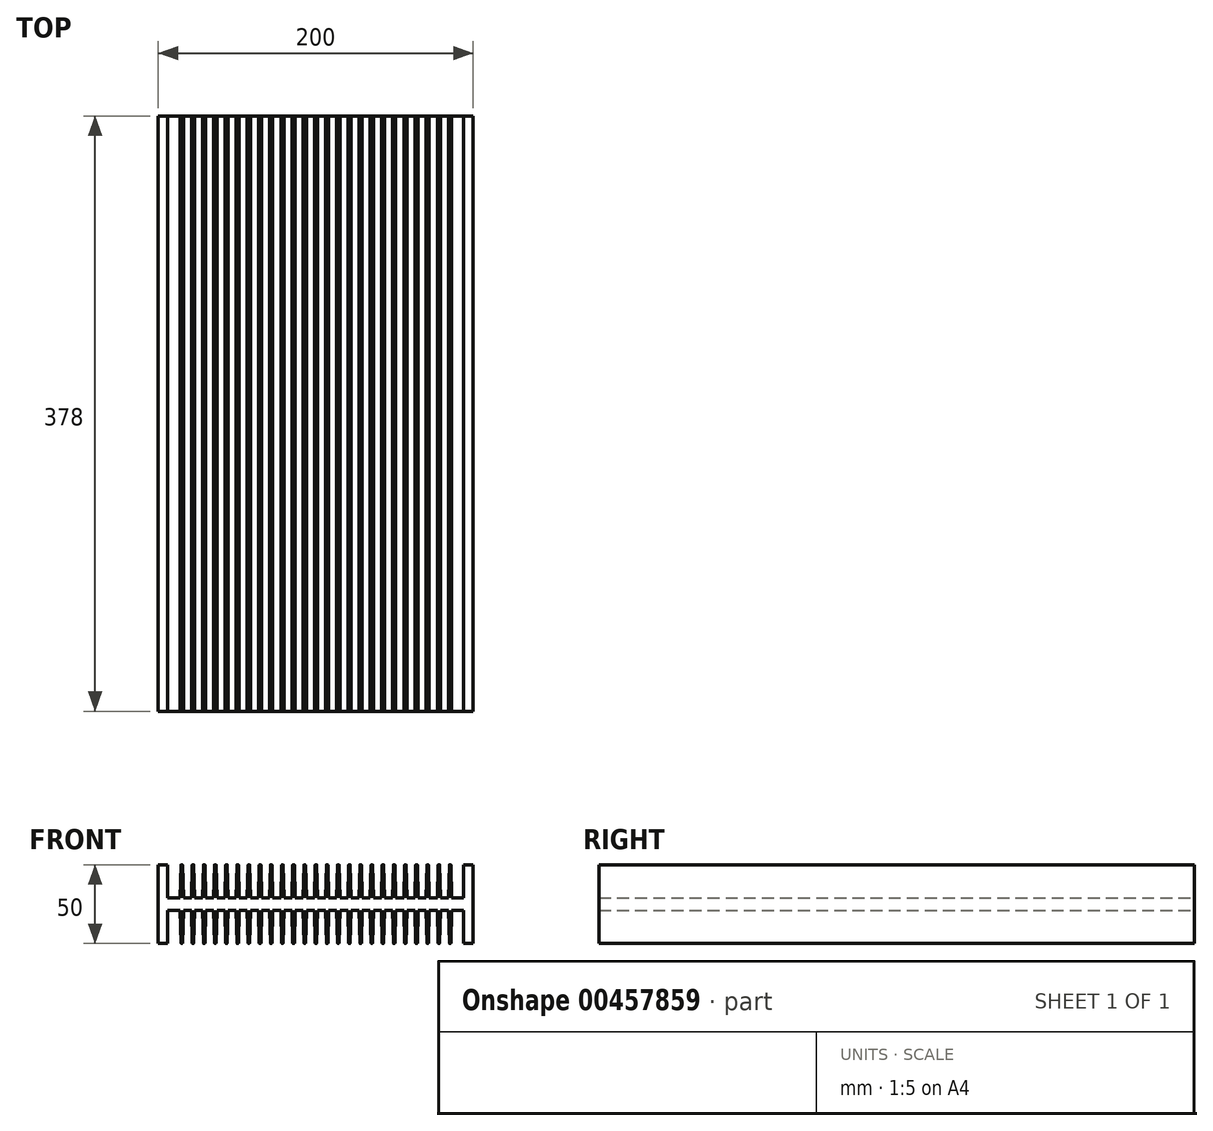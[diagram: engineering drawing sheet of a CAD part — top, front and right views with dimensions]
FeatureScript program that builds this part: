
annotation { "Feature Type Name" : "Feature", "Feature Type Description" : "" }
export const myFeature = defineFeature(function(context is Context, id is Id, definition is map)
    precondition{}
    {
        {
            var Q0;
            Q0=qCreatedBy(makeId("Front.planeOp"),FACE);
            var sketch = newSketch(context, id + "F0", { "sketchPlane" : qUnion([Q0])});
            skLineSegment(sketch, "E0", {"start": v(8, 0) * mm, "end": v(8.5, 20.88) * mm});
            skLineSegment(sketch, "E1", {"start": v(-6, 21) * mm, "end": v(-6, -4) * mm});
            skLineSegment(sketch, "E2", {"start": v(-6, -4) * mm, "end": v(194, -4) * mm});
            skLineSegment(sketch, "E3", {"start": v(194, 21) * mm, "end": v(194, -4) * mm});
            skLineSegment(sketch, "E4", {"start": v(9, 0) * mm, "end": v(9, 21) * mm});
            skLineSegment(sketch, "E5", {"start": v(9, 21) * mm, "end": v(9, 0) * mm, "construction": true});
            skPoint(sketch, "E6.visualSharp", {"position": v(8.5, 21) * mm});
            skArc(sketch, "E6.filletArc", {"start": v(8.62, 21) * mm, "mid": v(8.53, 20.97) * mm, "end": v(8.5, 20.88) * mm});
            skPoint(sketch, "E7.visualSharp", {"position": v(9.5, 21) * mm});
            skLineSegment(sketch, "E8", {"start": v(0, 0) * mm, "end": v(8, 0) * mm});
            skLineSegment(sketch, "E9", {"start": v(10, 0) * mm, "end": v(9.5, 20.88) * mm});
            skLineSegment(sketch, "E10", {"start": v(8.62, 21) * mm, "end": v(9.38, 21) * mm});
            skArc(sketch, "E11.filletArc", {"start": v(9.5, 20.88) * mm, "mid": v(9.47, 20.96) * mm, "end": v(9.38, 21) * mm});
            skLineSegment(sketch, "E12.1.0.1", {"start": v(15.1, 0) * mm, "end": v(15.6, 20.88) * mm});
            skArc(sketch, "E12.1.0.2", {"start": v(15.72, 21) * mm, "mid": v(15.63, 20.97) * mm, "end": v(15.6, 20.88) * mm});
            skLineSegment(sketch, "E12.1.0.3", {"start": v(15.72, 21) * mm, "end": v(16.48, 21) * mm});
            skArc(sketch, "E12.1.0.4", {"start": v(16.6, 20.88) * mm, "mid": v(16.57, 20.96) * mm, "end": v(16.48, 21) * mm});
            skLineSegment(sketch, "E12.1.0.5", {"start": v(17.1, 0) * mm, "end": v(16.6, 20.88) * mm});
            skLineSegment(sketch, "E12.2.0.1", {"start": v(22.2, 0) * mm, "end": v(22.7, 20.88) * mm});
            skArc(sketch, "E12.2.0.2", {"start": v(22.82, 21) * mm, "mid": v(22.73, 20.97) * mm, "end": v(22.7, 20.88) * mm});
            skLineSegment(sketch, "E12.2.0.3", {"start": v(22.82, 21) * mm, "end": v(23.58, 21) * mm});
            skArc(sketch, "E12.2.0.4", {"start": v(23.7, 20.88) * mm, "mid": v(23.67, 20.96) * mm, "end": v(23.58, 21) * mm});
            skLineSegment(sketch, "E12.2.0.5", {"start": v(24.2, 0) * mm, "end": v(23.7, 20.88) * mm});
            skLineSegment(sketch, "E12.3.0.1", {"start": v(29.3, 0) * mm, "end": v(29.8, 20.88) * mm});
            skArc(sketch, "E12.3.0.2", {"start": v(29.92, 21) * mm, "mid": v(29.83, 20.97) * mm, "end": v(29.8, 20.88) * mm});
            skLineSegment(sketch, "E12.3.0.3", {"start": v(29.92, 21) * mm, "end": v(30.68, 21) * mm});
            skArc(sketch, "E12.3.0.4", {"start": v(30.8, 20.88) * mm, "mid": v(30.77, 20.96) * mm, "end": v(30.68, 21) * mm});
            skLineSegment(sketch, "E12.3.0.5", {"start": v(31.3, 0) * mm, "end": v(30.8, 20.88) * mm});
            skLineSegment(sketch, "E12.4.0.1", {"start": v(36.4, 0) * mm, "end": v(36.9, 20.88) * mm});
            skArc(sketch, "E12.4.0.2", {"start": v(37.02, 21) * mm, "mid": v(36.93, 20.97) * mm, "end": v(36.9, 20.88) * mm});
            skLineSegment(sketch, "E12.4.0.3", {"start": v(37.02, 21) * mm, "end": v(37.78, 21) * mm});
            skArc(sketch, "E12.4.0.4", {"start": v(37.9, 20.88) * mm, "mid": v(37.87, 20.96) * mm, "end": v(37.78, 21) * mm});
            skLineSegment(sketch, "E12.4.0.5", {"start": v(38.4, 0) * mm, "end": v(37.9, 20.88) * mm});
            skLineSegment(sketch, "E12.5.0.1", {"start": v(43.5, 0) * mm, "end": v(44, 20.88) * mm});
            skArc(sketch, "E12.5.0.2", {"start": v(44.12, 21) * mm, "mid": v(44.03, 20.97) * mm, "end": v(44, 20.88) * mm});
            skLineSegment(sketch, "E12.5.0.3", {"start": v(44.12, 21) * mm, "end": v(44.88, 21) * mm});
            skArc(sketch, "E12.5.0.4", {"start": v(45, 20.88) * mm, "mid": v(44.97, 20.96) * mm, "end": v(44.88, 21) * mm});
            skLineSegment(sketch, "E12.5.0.5", {"start": v(45.5, 0) * mm, "end": v(45, 20.88) * mm});
            skLineSegment(sketch, "E12.6.0.1", {"start": v(50.6, 0) * mm, "end": v(51.1, 20.88) * mm});
            skArc(sketch, "E12.6.0.2", {"start": v(51.22, 21) * mm, "mid": v(51.13, 20.97) * mm, "end": v(51.1, 20.88) * mm});
            skLineSegment(sketch, "E12.6.0.3", {"start": v(51.22, 21) * mm, "end": v(51.98, 21) * mm});
            skArc(sketch, "E12.6.0.4", {"start": v(52.1, 20.88) * mm, "mid": v(52.07, 20.96) * mm, "end": v(51.98, 21) * mm});
            skLineSegment(sketch, "E12.6.0.5", {"start": v(52.6, 0) * mm, "end": v(52.1, 20.88) * mm});
            skLineSegment(sketch, "E12.7.0.1", {"start": v(57.7, 0) * mm, "end": v(58.2, 20.88) * mm});
            skArc(sketch, "E12.7.0.2", {"start": v(58.32, 21) * mm, "mid": v(58.23, 20.97) * mm, "end": v(58.2, 20.88) * mm});
            skLineSegment(sketch, "E12.7.0.3", {"start": v(58.32, 21) * mm, "end": v(59.08, 21) * mm});
            skArc(sketch, "E12.7.0.4", {"start": v(59.2, 20.88) * mm, "mid": v(59.17, 20.96) * mm, "end": v(59.08, 21) * mm});
            skLineSegment(sketch, "E12.7.0.5", {"start": v(59.7, 0) * mm, "end": v(59.2, 20.88) * mm});
            skLineSegment(sketch, "E12.8.0.1", {"start": v(64.8, 0) * mm, "end": v(65.3, 20.88) * mm});
            skArc(sketch, "E12.8.0.2", {"start": v(65.42, 21) * mm, "mid": v(65.33, 20.97) * mm, "end": v(65.3, 20.88) * mm});
            skLineSegment(sketch, "E12.8.0.3", {"start": v(65.42, 21) * mm, "end": v(66.18, 21) * mm});
            skArc(sketch, "E12.8.0.4", {"start": v(66.3, 20.88) * mm, "mid": v(66.27, 20.96) * mm, "end": v(66.18, 21) * mm});
            skLineSegment(sketch, "E12.8.0.5", {"start": v(66.8, 0) * mm, "end": v(66.3, 20.88) * mm});
            skLineSegment(sketch, "E12.9.0.1", {"start": v(71.9, 0) * mm, "end": v(72.4, 20.88) * mm});
            skArc(sketch, "E12.9.0.2", {"start": v(72.52, 21) * mm, "mid": v(72.43, 20.97) * mm, "end": v(72.4, 20.88) * mm});
            skLineSegment(sketch, "E12.9.0.3", {"start": v(72.52, 21) * mm, "end": v(73.28, 21) * mm});
            skArc(sketch, "E12.9.0.4", {"start": v(73.4, 20.88) * mm, "mid": v(73.37, 20.96) * mm, "end": v(73.28, 21) * mm});
            skLineSegment(sketch, "E12.9.0.5", {"start": v(73.9, 0) * mm, "end": v(73.4, 20.88) * mm});
            skLineSegment(sketch, "E13", {"start": v(-6, 21) * mm, "end": v(0, 21) * mm});
            skLineSegment(sketch, "E14", {"start": v(0, 21) * mm, "end": v(0, 0) * mm});
            skLineSegment(sketch, "E15", {"start": v(188, 0) * mm, "end": v(188, 21) * mm});
            skLineSegment(sketch, "E16", {"start": v(188, 21) * mm, "end": v(194, 21) * mm});
            skLineSegment(sketch, "E17.3.10.0", {"start": v(79, 0) * mm, "end": v(79.5, 20.88) * mm});
            skArc(sketch, "E17.6.10.0", {"start": v(79.62, 21) * mm, "mid": v(79.53, 20.97) * mm, "end": v(79.5, 20.88) * mm});
            skLineSegment(sketch, "E17.10.10.0", {"start": v(79.62, 21) * mm, "end": v(80.38, 21) * mm});
            skArc(sketch, "E17.13.10.0", {"start": v(80.5, 20.88) * mm, "mid": v(80.47, 20.96) * mm, "end": v(80.38, 21) * mm});
            skLineSegment(sketch, "E17.17.10.0", {"start": v(81, 0) * mm, "end": v(80.5, 20.88) * mm});
            skLineSegment(sketch, "E17.3.11.0", {"start": v(86.1, 0) * mm, "end": v(86.6, 20.88) * mm});
            skArc(sketch, "E17.6.11.0", {"start": v(86.72, 21) * mm, "mid": v(86.63, 20.97) * mm, "end": v(86.6, 20.88) * mm});
            skLineSegment(sketch, "E17.10.11.0", {"start": v(86.72, 21) * mm, "end": v(87.48, 21) * mm});
            skArc(sketch, "E17.13.11.0", {"start": v(87.6, 20.88) * mm, "mid": v(87.57, 20.96) * mm, "end": v(87.48, 21) * mm});
            skLineSegment(sketch, "E17.17.11.0", {"start": v(88.1, 0) * mm, "end": v(87.6, 20.88) * mm});
            skLineSegment(sketch, "E17.3.12.0", {"start": v(93.2, 0) * mm, "end": v(93.7, 20.88) * mm});
            skArc(sketch, "E17.6.12.0", {"start": v(93.82, 21) * mm, "mid": v(93.73, 20.97) * mm, "end": v(93.7, 20.88) * mm});
            skLineSegment(sketch, "E17.10.12.0", {"start": v(93.82, 21) * mm, "end": v(94.58, 21) * mm});
            skArc(sketch, "E17.13.12.0", {"start": v(94.7, 20.88) * mm, "mid": v(94.67, 20.96) * mm, "end": v(94.58, 21) * mm});
            skLineSegment(sketch, "E17.17.12.0", {"start": v(95.2, 0) * mm, "end": v(94.7, 20.88) * mm});
            skLineSegment(sketch, "E17.3.13.0", {"start": v(100.3, 0) * mm, "end": v(100.8, 20.88) * mm});
            skArc(sketch, "E17.6.13.0", {"start": v(100.92, 21) * mm, "mid": v(100.83, 20.97) * mm, "end": v(100.8, 20.88) * mm});
            skLineSegment(sketch, "E17.10.13.0", {"start": v(100.92, 21) * mm, "end": v(101.68, 21) * mm});
            skArc(sketch, "E17.13.13.0", {"start": v(101.8, 20.88) * mm, "mid": v(101.77, 20.96) * mm, "end": v(101.68, 21) * mm});
            skLineSegment(sketch, "E17.17.13.0", {"start": v(102.3, 0) * mm, "end": v(101.8, 20.88) * mm});
            skLineSegment(sketch, "E17.3.14.0", {"start": v(107.4, 0) * mm, "end": v(107.9, 20.88) * mm});
            skArc(sketch, "E17.6.14.0", {"start": v(108.02, 21) * mm, "mid": v(107.93, 20.97) * mm, "end": v(107.9, 20.88) * mm});
            skLineSegment(sketch, "E17.10.14.0", {"start": v(108.02, 21) * mm, "end": v(108.78, 21) * mm});
            skArc(sketch, "E17.13.14.0", {"start": v(108.9, 20.88) * mm, "mid": v(108.87, 20.96) * mm, "end": v(108.78, 21) * mm});
            skLineSegment(sketch, "E17.17.14.0", {"start": v(109.4, 0) * mm, "end": v(108.9, 20.88) * mm});
            skLineSegment(sketch, "E17.3.15.0", {"start": v(114.5, 0) * mm, "end": v(115, 20.88) * mm});
            skArc(sketch, "E17.6.15.0", {"start": v(115.12, 21) * mm, "mid": v(115.03, 20.97) * mm, "end": v(115, 20.88) * mm});
            skLineSegment(sketch, "E17.10.15.0", {"start": v(115.12, 21) * mm, "end": v(115.88, 21) * mm});
            skArc(sketch, "E17.13.15.0", {"start": v(116, 20.88) * mm, "mid": v(115.97, 20.96) * mm, "end": v(115.88, 21) * mm});
            skLineSegment(sketch, "E17.17.15.0", {"start": v(116.5, 0) * mm, "end": v(116, 20.88) * mm});
            skLineSegment(sketch, "E17.3.16.0", {"start": v(121.6, 0) * mm, "end": v(122.1, 20.88) * mm});
            skArc(sketch, "E17.6.16.0", {"start": v(122.22, 21) * mm, "mid": v(122.13, 20.97) * mm, "end": v(122.1, 20.88) * mm});
            skLineSegment(sketch, "E17.10.16.0", {"start": v(122.22, 21) * mm, "end": v(122.98, 21) * mm});
            skArc(sketch, "E17.13.16.0", {"start": v(123.1, 20.88) * mm, "mid": v(123.07, 20.96) * mm, "end": v(122.98, 21) * mm});
            skLineSegment(sketch, "E17.17.16.0", {"start": v(123.6, 0) * mm, "end": v(123.1, 20.88) * mm});
            skLineSegment(sketch, "E17.3.17.0", {"start": v(128.7, 0) * mm, "end": v(129.2, 20.88) * mm});
            skArc(sketch, "E17.6.17.0", {"start": v(129.32, 21) * mm, "mid": v(129.23, 20.97) * mm, "end": v(129.2, 20.88) * mm});
            skLineSegment(sketch, "E17.10.17.0", {"start": v(129.32, 21) * mm, "end": v(130.08, 21) * mm});
            skArc(sketch, "E17.13.17.0", {"start": v(130.2, 20.88) * mm, "mid": v(130.17, 20.96) * mm, "end": v(130.08, 21) * mm});
            skLineSegment(sketch, "E17.17.17.0", {"start": v(130.7, 0) * mm, "end": v(130.2, 20.88) * mm});
            skLineSegment(sketch, "E18.3.18.0", {"start": v(135.8, 0) * mm, "end": v(136.3, 20.88) * mm});
            skArc(sketch, "E18.6.18.0", {"start": v(136.42, 21) * mm, "mid": v(136.33, 20.97) * mm, "end": v(136.3, 20.88) * mm});
            skLineSegment(sketch, "E18.10.18.0", {"start": v(136.42, 21) * mm, "end": v(137.18, 21) * mm});
            skArc(sketch, "E18.13.18.0", {"start": v(137.3, 20.88) * mm, "mid": v(137.27, 20.96) * mm, "end": v(137.18, 21) * mm});
            skLineSegment(sketch, "E18.17.18.0", {"start": v(137.8, 0) * mm, "end": v(137.3, 20.88) * mm});
            skLineSegment(sketch, "E18.3.19.0", {"start": v(142.9, 0) * mm, "end": v(143.4, 20.88) * mm});
            skArc(sketch, "E18.6.19.0", {"start": v(143.52, 21) * mm, "mid": v(143.43, 20.97) * mm, "end": v(143.4, 20.88) * mm});
            skLineSegment(sketch, "E18.10.19.0", {"start": v(143.52, 21) * mm, "end": v(144.28, 21) * mm});
            skArc(sketch, "E18.13.19.0", {"start": v(144.4, 20.88) * mm, "mid": v(144.37, 20.96) * mm, "end": v(144.28, 21) * mm});
            skLineSegment(sketch, "E18.17.19.0", {"start": v(144.9, 0) * mm, "end": v(144.4, 20.88) * mm});
            skLineSegment(sketch, "E18.3.20.0", {"start": v(150, 0) * mm, "end": v(150.5, 20.88) * mm});
            skArc(sketch, "E18.6.20.0", {"start": v(150.62, 21) * mm, "mid": v(150.53, 20.97) * mm, "end": v(150.5, 20.88) * mm});
            skLineSegment(sketch, "E18.10.20.0", {"start": v(150.62, 21) * mm, "end": v(151.38, 21) * mm});
            skArc(sketch, "E18.13.20.0", {"start": v(151.5, 20.88) * mm, "mid": v(151.47, 20.96) * mm, "end": v(151.38, 21) * mm});
            skLineSegment(sketch, "E18.17.20.0", {"start": v(152, 0) * mm, "end": v(151.5, 20.88) * mm});
            skLineSegment(sketch, "E18.3.21.0", {"start": v(157.1, 0) * mm, "end": v(157.6, 20.88) * mm});
            skArc(sketch, "E18.6.21.0", {"start": v(157.72, 21) * mm, "mid": v(157.63, 20.97) * mm, "end": v(157.6, 20.88) * mm});
            skLineSegment(sketch, "E18.10.21.0", {"start": v(157.72, 21) * mm, "end": v(158.48, 21) * mm});
            skArc(sketch, "E18.13.21.0", {"start": v(158.6, 20.88) * mm, "mid": v(158.57, 20.96) * mm, "end": v(158.48, 21) * mm});
            skLineSegment(sketch, "E18.17.21.0", {"start": v(159.1, 0) * mm, "end": v(158.6, 20.88) * mm});
            skLineSegment(sketch, "E18.3.22.0", {"start": v(164.2, 0) * mm, "end": v(164.7, 20.88) * mm});
            skArc(sketch, "E18.6.22.0", {"start": v(164.82, 21) * mm, "mid": v(164.73, 20.97) * mm, "end": v(164.7, 20.88) * mm});
            skLineSegment(sketch, "E18.10.22.0", {"start": v(164.82, 21) * mm, "end": v(165.58, 21) * mm});
            skArc(sketch, "E18.13.22.0", {"start": v(165.7, 20.88) * mm, "mid": v(165.67, 20.96) * mm, "end": v(165.58, 21) * mm});
            skLineSegment(sketch, "E18.17.22.0", {"start": v(166.2, 0) * mm, "end": v(165.7, 20.88) * mm});
            skLineSegment(sketch, "E18.3.23.0", {"start": v(171.3, 0) * mm, "end": v(171.8, 20.88) * mm});
            skArc(sketch, "E18.6.23.0", {"start": v(171.92, 21) * mm, "mid": v(171.83, 20.97) * mm, "end": v(171.8, 20.88) * mm});
            skLineSegment(sketch, "E18.10.23.0", {"start": v(171.92, 21) * mm, "end": v(172.68, 21) * mm});
            skArc(sketch, "E18.13.23.0", {"start": v(172.8, 20.88) * mm, "mid": v(172.77, 20.96) * mm, "end": v(172.68, 21) * mm});
            skLineSegment(sketch, "E18.17.23.0", {"start": v(173.3, 0) * mm, "end": v(172.8, 20.88) * mm});
            skLineSegment(sketch, "E18.3.24.0", {"start": v(178.4, 0) * mm, "end": v(178.9, 20.88) * mm});
            skArc(sketch, "E18.6.24.0", {"start": v(179.02, 21) * mm, "mid": v(178.93, 20.97) * mm, "end": v(178.9, 20.88) * mm});
            skLineSegment(sketch, "E18.10.24.0", {"start": v(179.02, 21) * mm, "end": v(179.78, 21) * mm});
            skArc(sketch, "E18.13.24.0", {"start": v(179.9, 20.88) * mm, "mid": v(179.87, 20.96) * mm, "end": v(179.78, 21) * mm});
            skLineSegment(sketch, "E18.17.24.0", {"start": v(180.4, 0) * mm, "end": v(179.9, 20.88) * mm});
            skLineSegment(sketch, "E19", {"start": v(188, 0) * mm, "end": v(180.4, 0) * mm});
            skLineSegment(sketch, "E20", {"start": v(178.4, 0) * mm, "end": v(173.3, 0) * mm});
            skLineSegment(sketch, "E21", {"start": v(171.3, 0) * mm, "end": v(166.2, 0) * mm});
            skLineSegment(sketch, "E22", {"start": v(164.2, 0) * mm, "end": v(159.1, 0) * mm});
            skLineSegment(sketch, "E23", {"start": v(157.1, 0) * mm, "end": v(152, 0) * mm});
            skLineSegment(sketch, "E24", {"start": v(150, 0) * mm, "end": v(144.9, 0) * mm});
            skLineSegment(sketch, "E25", {"start": v(142.9, 0) * mm, "end": v(137.8, 0) * mm});
            skLineSegment(sketch, "E26", {"start": v(135.8, 0) * mm, "end": v(130.7, 0) * mm});
            skLineSegment(sketch, "E27", {"start": v(128.7, 0) * mm, "end": v(123.6, 0) * mm});
            skLineSegment(sketch, "E28", {"start": v(121.6, 0) * mm, "end": v(116.5, 0) * mm});
            skLineSegment(sketch, "E29", {"start": v(114.5, 0) * mm, "end": v(109.4, 0) * mm});
            skLineSegment(sketch, "E30", {"start": v(107.4, 0) * mm, "end": v(102.3, 0) * mm});
            skLineSegment(sketch, "E31", {"start": v(100.3, 0) * mm, "end": v(95.2, 0) * mm});
            skLineSegment(sketch, "E32", {"start": v(88.1, 0) * mm, "end": v(93.2, 0) * mm});
            skLineSegment(sketch, "E33", {"start": v(86.1, 0) * mm, "end": v(81, 0) * mm});
            skLineSegment(sketch, "E34", {"start": v(79, 0) * mm, "end": v(73.9, 0) * mm});
            skLineSegment(sketch, "E35", {"start": v(71.9, 0) * mm, "end": v(66.8, 0) * mm});
            skLineSegment(sketch, "E36", {"start": v(64.8, 0) * mm, "end": v(59.7, 0) * mm});
            skLineSegment(sketch, "E37", {"start": v(57.7, 0) * mm, "end": v(52.6, 0) * mm});
            skLineSegment(sketch, "E38", {"start": v(50.6, 0) * mm, "end": v(45.5, 0) * mm});
            skLineSegment(sketch, "E39", {"start": v(43.5, 0) * mm, "end": v(38.4, 0) * mm});
            skLineSegment(sketch, "E40", {"start": v(36.4, 0) * mm, "end": v(31.3, 0) * mm});
            skLineSegment(sketch, "E41", {"start": v(29.3, 0) * mm, "end": v(24.2, 0) * mm});
            skLineSegment(sketch, "E42", {"start": v(22.2, 0) * mm, "end": v(17.1, 0) * mm});
            skLineSegment(sketch, "E43", {"start": v(15.1, 0) * mm, "end": v(10, 0) * mm});
            skSolve(sketch);
        }
        {
            var Q0;
            Q0=qSketchRegion(id+"F0",true);
            extrude(context, id + "F1", {"entities" : qUnion([Q0]), "depth" : 378 * mm});
        }
        {
            var Q0;
            Q0=makeQuery(id+"F1.opExtrude","SWEPT_BODY",BODY,{"disambiguationData":[OSD([sQuery(id+"F0.wireOp",EDGE,"E0"),sQuery(id+"F0.wireOp",EDGE,"E1"),sQuery(id+"F0.wireOp",EDGE,"E2"),sQuery(id+"F0.wireOp",EDGE,"E3"),sQuery(id+"F0.wireOp",EDGE,"E6.filletArc"),sQuery(id+"F0.wireOp",EDGE,"E8"),sQuery(id+"F0.wireOp",EDGE,"E9"),sQuery(id+"F0.wireOp",EDGE,"E10"),sQuery(id+"F0.wireOp",EDGE,"E11.filletArc"),sQuery(id+"F0.wireOp",EDGE,"E12.1.0.1"),sQuery(id+"F0.wireOp",EDGE,"E12.1.0.2"),sQuery(id+"F0.wireOp",EDGE,"E12.1.0.3"),sQuery(id+"F0.wireOp",EDGE,"E12.1.0.4"),sQuery(id+"F0.wireOp",EDGE,"E12.1.0.5"),sQuery(id+"F0.wireOp",EDGE,"E12.2.0.1"),sQuery(id+"F0.wireOp",EDGE,"E12.2.0.2"),sQuery(id+"F0.wireOp",EDGE,"E12.2.0.3"),sQuery(id+"F0.wireOp",EDGE,"E12.2.0.4"),sQuery(id+"F0.wireOp",EDGE,"E12.2.0.5"),sQuery(id+"F0.wireOp",EDGE,"E12.3.0.1"),sQuery(id+"F0.wireOp",EDGE,"E12.3.0.2"),sQuery(id+"F0.wireOp",EDGE,"E12.3.0.3"),sQuery(id+"F0.wireOp",EDGE,"E12.3.0.4"),sQuery(id+"F0.wireOp",EDGE,"E12.3.0.5"),sQuery(id+"F0.wireOp",EDGE,"E12.4.0.1"),sQuery(id+"F0.wireOp",EDGE,"E12.4.0.2"),sQuery(id+"F0.wireOp",EDGE,"E12.4.0.3"),sQuery(id+"F0.wireOp",EDGE,"E12.4.0.4"),sQuery(id+"F0.wireOp",EDGE,"E12.4.0.5"),sQuery(id+"F0.wireOp",EDGE,"E12.5.0.1"),sQuery(id+"F0.wireOp",EDGE,"E12.5.0.2"),sQuery(id+"F0.wireOp",EDGE,"E12.5.0.3"),sQuery(id+"F0.wireOp",EDGE,"E12.5.0.4"),sQuery(id+"F0.wireOp",EDGE,"E12.5.0.5"),sQuery(id+"F0.wireOp",EDGE,"E12.6.0.1"),sQuery(id+"F0.wireOp",EDGE,"E12.6.0.2"),sQuery(id+"F0.wireOp",EDGE,"E12.6.0.3"),sQuery(id+"F0.wireOp",EDGE,"E12.6.0.4"),sQuery(id+"F0.wireOp",EDGE,"E12.6.0.5"),sQuery(id+"F0.wireOp",EDGE,"E12.7.0.1"),sQuery(id+"F0.wireOp",EDGE,"E12.7.0.2"),sQuery(id+"F0.wireOp",EDGE,"E12.7.0.3"),sQuery(id+"F0.wireOp",EDGE,"E12.7.0.4"),sQuery(id+"F0.wireOp",EDGE,"E12.7.0.5"),sQuery(id+"F0.wireOp",EDGE,"E12.8.0.1"),sQuery(id+"F0.wireOp",EDGE,"E12.8.0.2"),sQuery(id+"F0.wireOp",EDGE,"E12.8.0.3"),sQuery(id+"F0.wireOp",EDGE,"E12.8.0.4"),sQuery(id+"F0.wireOp",EDGE,"E12.8.0.5"),sQuery(id+"F0.wireOp",EDGE,"E12.9.0.1"),sQuery(id+"F0.wireOp",EDGE,"E12.9.0.2"),sQuery(id+"F0.wireOp",EDGE,"E12.9.0.3"),sQuery(id+"F0.wireOp",EDGE,"E12.9.0.4"),sQuery(id+"F0.wireOp",EDGE,"E12.9.0.5"),sQuery(id+"F0.wireOp",EDGE,"E13"),sQuery(id+"F0.wireOp",EDGE,"E14"),sQuery(id+"F0.wireOp",EDGE,"E15"),sQuery(id+"F0.wireOp",EDGE,"E16"),sQuery(id+"F0.wireOp",EDGE,"E17.3.10.0"),sQuery(id+"F0.wireOp",EDGE,"E17.6.10.0"),sQuery(id+"F0.wireOp",EDGE,"E17.10.10.0"),sQuery(id+"F0.wireOp",EDGE,"E17.13.10.0"),sQuery(id+"F0.wireOp",EDGE,"E17.17.10.0"),sQuery(id+"F0.wireOp",EDGE,"E17.3.11.0"),sQuery(id+"F0.wireOp",EDGE,"E17.6.11.0"),sQuery(id+"F0.wireOp",EDGE,"E17.10.11.0"),sQuery(id+"F0.wireOp",EDGE,"E17.13.11.0"),sQuery(id+"F0.wireOp",EDGE,"E17.17.11.0"),sQuery(id+"F0.wireOp",EDGE,"E17.3.12.0"),sQuery(id+"F0.wireOp",EDGE,"E17.6.12.0"),sQuery(id+"F0.wireOp",EDGE,"E17.10.12.0"),sQuery(id+"F0.wireOp",EDGE,"E17.13.12.0"),sQuery(id+"F0.wireOp",EDGE,"E17.17.12.0"),sQuery(id+"F0.wireOp",EDGE,"E17.3.13.0"),sQuery(id+"F0.wireOp",EDGE,"E17.6.13.0"),sQuery(id+"F0.wireOp",EDGE,"E17.10.13.0"),sQuery(id+"F0.wireOp",EDGE,"E17.13.13.0"),sQuery(id+"F0.wireOp",EDGE,"E17.17.13.0"),sQuery(id+"F0.wireOp",EDGE,"E17.3.14.0"),sQuery(id+"F0.wireOp",EDGE,"E17.6.14.0"),sQuery(id+"F0.wireOp",EDGE,"E17.10.14.0"),sQuery(id+"F0.wireOp",EDGE,"E17.13.14.0"),sQuery(id+"F0.wireOp",EDGE,"E17.17.14.0"),sQuery(id+"F0.wireOp",EDGE,"E17.3.15.0"),sQuery(id+"F0.wireOp",EDGE,"E17.6.15.0"),sQuery(id+"F0.wireOp",EDGE,"E17.10.15.0"),sQuery(id+"F0.wireOp",EDGE,"E17.13.15.0"),sQuery(id+"F0.wireOp",EDGE,"E17.17.15.0"),sQuery(id+"F0.wireOp",EDGE,"E17.3.16.0"),sQuery(id+"F0.wireOp",EDGE,"E17.6.16.0"),sQuery(id+"F0.wireOp",EDGE,"E17.10.16.0"),sQuery(id+"F0.wireOp",EDGE,"E17.13.16.0"),sQuery(id+"F0.wireOp",EDGE,"E17.17.16.0"),sQuery(id+"F0.wireOp",EDGE,"E17.3.17.0"),sQuery(id+"F0.wireOp",EDGE,"E17.6.17.0"),sQuery(id+"F0.wireOp",EDGE,"E17.10.17.0"),sQuery(id+"F0.wireOp",EDGE,"E17.13.17.0"),sQuery(id+"F0.wireOp",EDGE,"E17.17.17.0"),sQuery(id+"F0.wireOp",EDGE,"E18.3.18.0"),sQuery(id+"F0.wireOp",EDGE,"E18.6.18.0"),sQuery(id+"F0.wireOp",EDGE,"E18.10.18.0"),sQuery(id+"F0.wireOp",EDGE,"E18.13.18.0"),sQuery(id+"F0.wireOp",EDGE,"E18.17.18.0"),sQuery(id+"F0.wireOp",EDGE,"E18.3.19.0"),sQuery(id+"F0.wireOp",EDGE,"E18.6.19.0"),sQuery(id+"F0.wireOp",EDGE,"E18.10.19.0"),sQuery(id+"F0.wireOp",EDGE,"E18.13.19.0"),sQuery(id+"F0.wireOp",EDGE,"E18.17.19.0"),sQuery(id+"F0.wireOp",EDGE,"E18.3.20.0"),sQuery(id+"F0.wireOp",EDGE,"E18.6.20.0"),sQuery(id+"F0.wireOp",EDGE,"E18.10.20.0"),sQuery(id+"F0.wireOp",EDGE,"E18.13.20.0"),sQuery(id+"F0.wireOp",EDGE,"E18.17.20.0"),sQuery(id+"F0.wireOp",EDGE,"E18.3.21.0"),sQuery(id+"F0.wireOp",EDGE,"E18.6.21.0"),sQuery(id+"F0.wireOp",EDGE,"E18.10.21.0"),sQuery(id+"F0.wireOp",EDGE,"E18.13.21.0"),sQuery(id+"F0.wireOp",EDGE,"E18.17.21.0"),sQuery(id+"F0.wireOp",EDGE,"E18.3.22.0"),sQuery(id+"F0.wireOp",EDGE,"E18.6.22.0"),sQuery(id+"F0.wireOp",EDGE,"E18.10.22.0"),sQuery(id+"F0.wireOp",EDGE,"E18.13.22.0"),sQuery(id+"F0.wireOp",EDGE,"E18.17.22.0"),sQuery(id+"F0.wireOp",EDGE,"E18.3.23.0"),sQuery(id+"F0.wireOp",EDGE,"E18.6.23.0"),sQuery(id+"F0.wireOp",EDGE,"E18.10.23.0"),sQuery(id+"F0.wireOp",EDGE,"E18.13.23.0"),sQuery(id+"F0.wireOp",EDGE,"E18.17.23.0"),sQuery(id+"F0.wireOp",EDGE,"E18.3.24.0"),sQuery(id+"F0.wireOp",EDGE,"E18.6.24.0"),sQuery(id+"F0.wireOp",EDGE,"E18.10.24.0"),sQuery(id+"F0.wireOp",EDGE,"E18.13.24.0"),sQuery(id+"F0.wireOp",EDGE,"E18.17.24.0"),sQuery(id+"F0.wireOp",EDGE,"E19"),sQuery(id+"F0.wireOp",EDGE,"E20"),sQuery(id+"F0.wireOp",EDGE,"E21"),sQuery(id+"F0.wireOp",EDGE,"E22"),sQuery(id+"F0.wireOp",EDGE,"E23"),sQuery(id+"F0.wireOp",EDGE,"E24"),sQuery(id+"F0.wireOp",EDGE,"E25"),sQuery(id+"F0.wireOp",EDGE,"E26"),sQuery(id+"F0.wireOp",EDGE,"E27"),sQuery(id+"F0.wireOp",EDGE,"E28"),sQuery(id+"F0.wireOp",EDGE,"E29"),sQuery(id+"F0.wireOp",EDGE,"E30"),sQuery(id+"F0.wireOp",EDGE,"E31"),sQuery(id+"F0.wireOp",EDGE,"E32"),sQuery(id+"F0.wireOp",EDGE,"E33"),sQuery(id+"F0.wireOp",EDGE,"E34"),sQuery(id+"F0.wireOp",EDGE,"E35"),sQuery(id+"F0.wireOp",EDGE,"E36"),sQuery(id+"F0.wireOp",EDGE,"E37"),sQuery(id+"F0.wireOp",EDGE,"E38"),sQuery(id+"F0.wireOp",EDGE,"E39"),sQuery(id+"F0.wireOp",EDGE,"E40"),sQuery(id+"F0.wireOp",EDGE,"E41"),sQuery(id+"F0.wireOp",EDGE,"E42"),sQuery(id+"F0.wireOp",EDGE,"E43")])]});
            var Q1;
            Q1=makeQuery(id+"F1.opExtrude","SWEPT_FACE",FACE,{"disambiguationData":[OSD([sQuery(id+"F0.wireOp",EDGE,"E2")])]});
            mirror(context, id + "F2", {"operationType" : NewBodyOperationType.ADD, "entities" : qUnion([Q0]), "mirrorPlane" : qUnion([Q1])});
        }
    });
